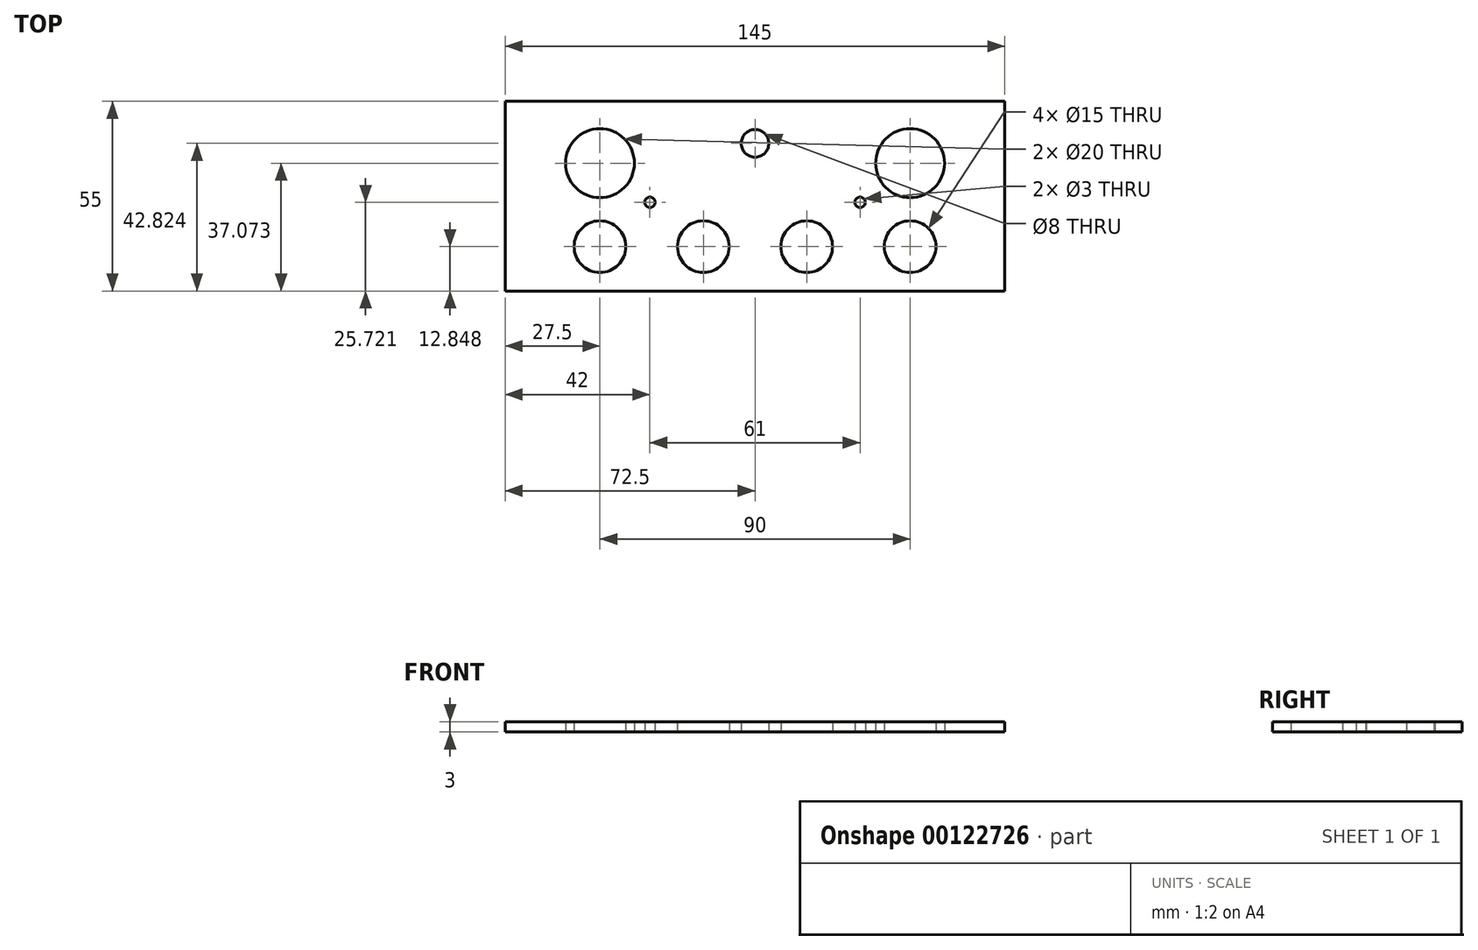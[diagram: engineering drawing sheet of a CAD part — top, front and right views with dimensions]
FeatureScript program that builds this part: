
annotation { "Feature Type Name" : "Feature", "Feature Type Description" : "" }
export const myFeature = defineFeature(function(context is Context, id is Id, definition is map)
    precondition{}
    {
        {
            var Q0;
            Q0=qCreatedBy(makeId("Top.planeOp"),FACE);
            var sketch = newSketch(context, id + "F0", { "sketchPlane" : qUnion([Q0])});
            skLineSegment(sketch, "E0.bottom", {"start": v(0, 0) * mm, "end": v(145, 0) * mm});
            skLineSegment(sketch, "E0.top", {"start": v(0, -55) * mm, "end": v(145, -55) * mm});
            skLineSegment(sketch, "E0.left", {"start": v(0, 0) * mm, "end": v(0, -55) * mm});
            skLineSegment(sketch, "E0.right", {"start": v(145, 0) * mm, "end": v(145, -55) * mm});
            skCircle(sketch, "E1", {"center": v(27.5, -17.93) * mm, "radius": 10 * mm});
            skCircle(sketch, "E2", {"center": v(72.5, -12.18) * mm, "radius": 4 * mm});
            skCircle(sketch, "E3", {"center": v(117.5, -17.93) * mm, "radius": 10 * mm});
            skCircle(sketch, "E4", {"center": v(27.5, -42.15) * mm, "radius": 7.5 * mm});
            skCircle(sketch, "E5", {"center": v(57.5, -42.15) * mm, "radius": 7.5 * mm});
            skCircle(sketch, "E6", {"center": v(117.5, -42.15) * mm, "radius": 7.5 * mm});
            skCircle(sketch, "E7", {"center": v(87.5, -42.15) * mm, "radius": 7.5 * mm});
            skCircle(sketch, "E8", {"center": v(103, -29.28) * mm, "radius": 1.5 * mm});
            skCircle(sketch, "E9", {"center": v(42, -29.28) * mm, "radius": 1.5 * mm});
            skSolve(sketch);
        }
        {
            var Q0;
            Q0=qSketchRegion(id+"F0",true);
            extrude(context, id + "F1", {"entities" : qUnion([Q0]), "depth" : 3 * mm});
        }
    });
